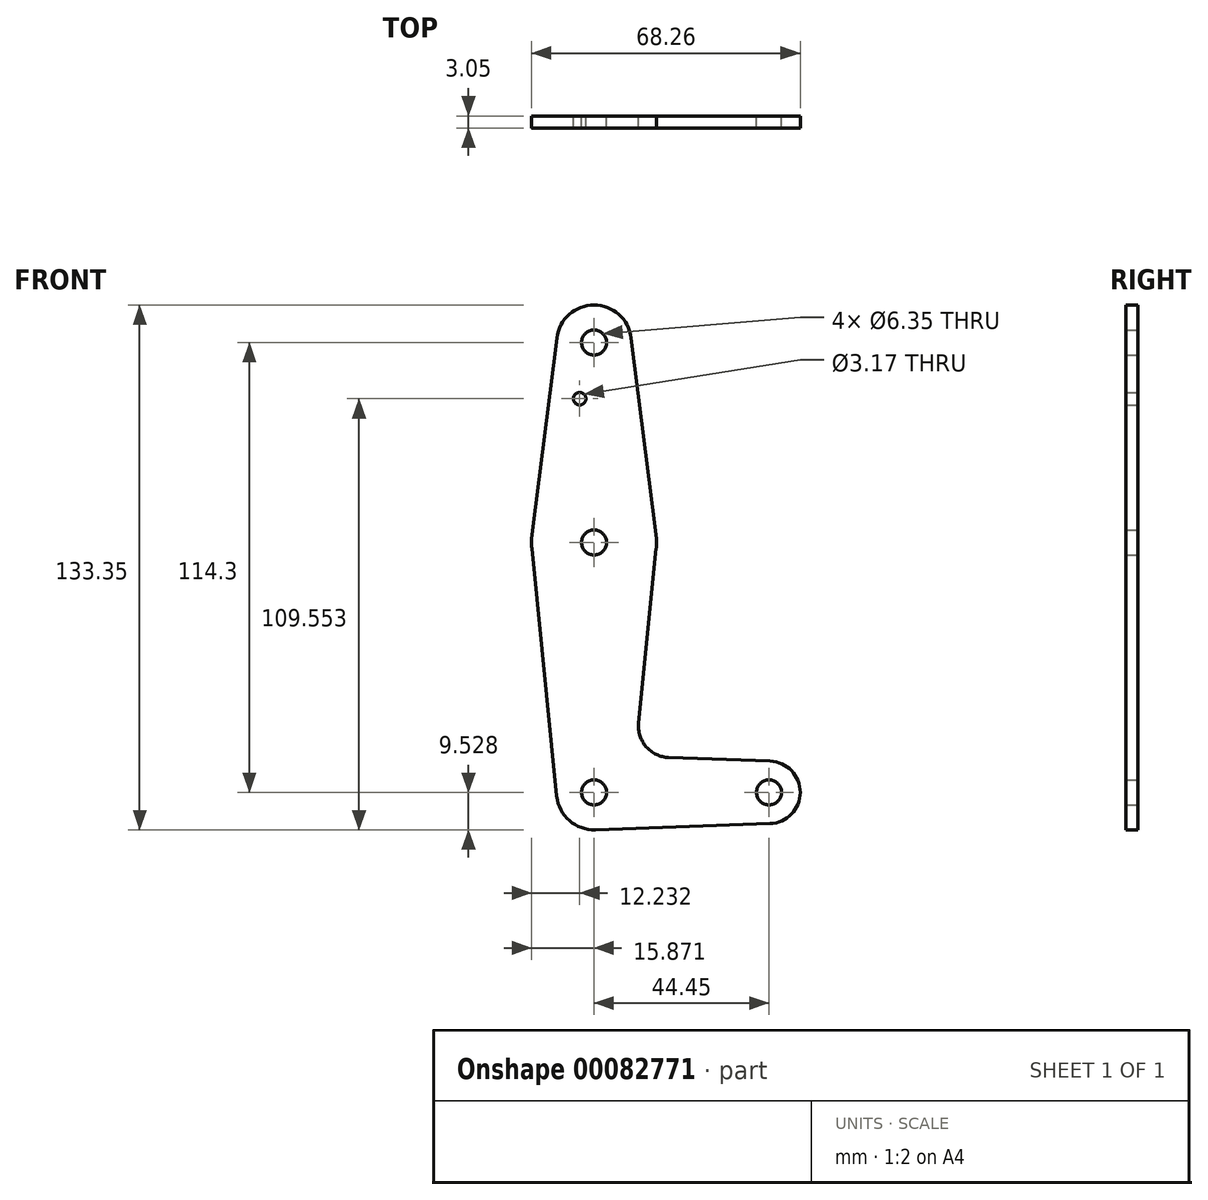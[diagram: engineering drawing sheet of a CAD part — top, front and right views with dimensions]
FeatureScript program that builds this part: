
annotation { "Feature Type Name" : "Feature", "Feature Type Description" : "" }
export const myFeature = defineFeature(function(context is Context, id is Id, definition is map)
    precondition{}
    {
        {
            var Q0;
            Q0=qCreatedBy(makeId("Front.planeOp"),FACE);
            var sketch = newSketch(context, id + "F0", { "sketchPlane" : qUnion([Q0])});
            skLineSegment(sketch, "E0", {"start": v(-17.76, 51.73) * mm, "end": v(-17.76, -62.57) * mm, "construction": true});
            skCircle(sketch, "E1", {"center": v(-17.76, 51.73) * mm, "radius": 9.53 * mm});
            skCircle(sketch, "E2", {"center": v(-17.76, -62.57) * mm, "radius": 9.53 * mm});
            skLineSegment(sketch, "E3", {"start": v(-17.76, -62.57) * mm, "end": v(-17.76, 0.93) * mm, "construction": true});
            skCircle(sketch, "E4", {"center": v(-17.76, 0.93) * mm, "radius": 15.88 * mm});
            skLineSegment(sketch, "E5", {"start": v(-17.76, -62.57) * mm, "end": v(26.7, -62.57) * mm, "construction": true});
            skCircle(sketch, "E6", {"center": v(26.7, -62.57) * mm, "radius": 7.94 * mm});
            skLineSegment(sketch, "E7", {"start": v(-27.2, 52.92) * mm, "end": v(-33.5, 2.91) * mm});
            skLineSegment(sketch, "E8", {"start": v(-8.3, 52.92) * mm, "end": v(-2, 2.91) * mm});
            skLineSegment(sketch, "E9", {"start": v(-33.55, -0.66) * mm, "end": v(-27.24, -63.52) * mm});
            skLineSegment(sketch, "E10", {"start": v(-1.96, -0.66) * mm, "end": v(-6.42, -44.98) * mm});
            skLineSegment(sketch, "E11", {"start": v(-17.42, -72.1) * mm, "end": v(26.97, -70.5) * mm});
            skLineSegment(sketch, "E12", {"start": v(1.2, -53.72) * mm, "end": v(26.97, -54.64) * mm});
            skCircle(sketch, "E13", {"center": v(-17.76, 51.73) * mm, "radius": 3.18 * mm});
            skCircle(sketch, "E14", {"center": v(-17.76, 0.93) * mm, "radius": 3.18 * mm});
            skCircle(sketch, "E15", {"center": v(-17.76, -62.57) * mm, "radius": 3.18 * mm});
            skCircle(sketch, "E16", {"center": v(26.7, -62.57) * mm, "radius": 3.18 * mm});
            skLineSegment(sketch, "E17", {"start": v(-17.76, 0.93) * mm, "end": v(-17.76, 37.45) * mm, "construction": true});
            skCircle(sketch, "E18", {"center": v(-21.4, 37.45) * mm, "radius": 1.59 * mm});
            skArc(sketch, "E19.filletArc", {"start": v(-6.42, -44.98) * mm, "mid": v(-4.5, -51) * mm, "end": v(1.2, -53.72) * mm});
            skSolve(sketch);
        }
        {
            var Q0;
            Q0=makeQuery(id+"F0.imprint","IMPRINT",FACE,{"disambiguationData":[TD([[makeQuery(id+"F0.imprint","IMPRINT",EDGE,{"derivedFrom":sQuery(id+"F0.wireOp",EDGE,"E13")}),-1.0]])]});
            var Q1;
            {var subQ1=sQuery(id+"F0.wireOp",EDGE,"E7");Q1=makeQuery(id+"F0.imprint","IMPRINT",FACE,{"disambiguationData":[TD([[makeQuery(id+"F0.imprint","IMPRINT",EDGE,{"derivedFrom":subQ1}),1.0]])]});}
            var Q2;
            Q2=makeQuery(id+"F0.imprint","IMPRINT",FACE,{"disambiguationData":[TD([[makeQuery(id+"F0.imprint","IMPRINT",EDGE,{"derivedFrom":sQuery(id+"F0.wireOp",EDGE,"E14")}),-1.0]])]});
            var Q3;
            {var subQ3=sQuery(id+"F0.wireOp",EDGE,"E10");Q3=makeQuery(id+"F0.imprint","IMPRINT",FACE,{"disambiguationData":[TD([[makeQuery(id+"F0.imprint","IMPRINT",EDGE,{"derivedFrom":subQ3}),-1.0]])]});}
            var Q4;
            {var subQ0=sQuery(id+"F0.wireOp",EDGE,"E9");Q4=makeQuery(id+"F0.imprint","IMPRINT",FACE,{"disambiguationData":[TD([[makeQuery(id+"F0.imprint","IMPRINT",EDGE,{"derivedFrom":subQ0}),1.0]])]});}
            var Q5;
            Q5=makeQuery(id+"F0.imprint","IMPRINT",FACE,{"disambiguationData":[TD([[makeQuery(id+"F0.imprint","IMPRINT",EDGE,{"derivedFrom":sQuery(id+"F0.wireOp",EDGE,"E15")}),-1.0]])]});
            var Q6;
            Q6=makeQuery(id+"F0.imprint","IMPRINT",FACE,{"disambiguationData":[TD([[makeQuery(id+"F0.imprint","IMPRINT",EDGE,{"derivedFrom":sQuery(id+"F0.wireOp",EDGE,"E16")}),-1.0]])]});
            extrude(context, id + "F1", {"entities" : qUnion([Q0, Q1, Q2, Q3, Q4, Q5, Q6]), "depth" : 3.05 * mm});
        }
    });
